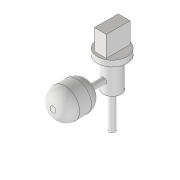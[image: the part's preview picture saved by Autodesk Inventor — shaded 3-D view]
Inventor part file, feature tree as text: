
AUTODESK INVENTOR PART (.ipt)
format: ipt  version: 2020 (Build 240168000, 168)  size: 146,432 bytes
history: native  units: mm
features: extrude x6, sketch x6, fillet x1
ambient origin geometry x8: Origin, YZ Plane, XZ Plane, XY Plane, X Axis, Y Axis, Z Axis, Center Point
bodies: Volumenkörper1 (feature_tree)
feature tree (13):
  extrude  "Extrusion1"  Depth=40.0mm
  extrude  "Extrusion2"  Depth=50.0mm
  extrude  "Extrusion3"  Depth=10.0mm
  extrude  "Extrusion4"  Depth=10.0mm
  extrude  "Extrusion5"  Depth=40.0mm
  fillet  "Rundung1"  Radius=50.0mm
  extrude  "Extrusion6"  Depth=20.0mm
  sketch  "Skizze1"  dims[d0=20.0mm d1=40.0mm]
  sketch  "Skizze2"  dims[d2=35.0mm d3=0.0mm d4=50.0mm]
  sketch  "Skizze3"  dims[d5=10.0mm d6=0.0mm d7=30.0mm]
  sketch  "Skizze4"  dims[d8=50.0mm d9=0.0mm d10=10.0mm]
  sketch  "Skizze5"  dims[d11=40.0mm d12=0.0mm d13=40.0mm d14=50.0mm]
  sketch  "Skizze6"  dims[d15=60.0mm d16=0.0mm d17=20.0mm d18=10.0mm d19=60.0mm d20=0.0mm]
